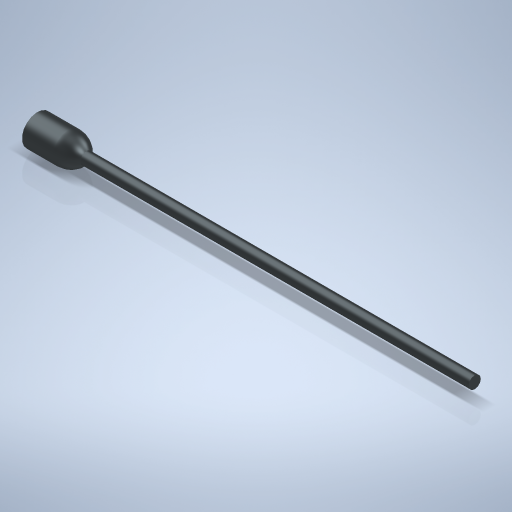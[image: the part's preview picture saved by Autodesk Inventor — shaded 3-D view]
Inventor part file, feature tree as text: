
AUTODESK INVENTOR PART (.ipt)
format: ipt  version: 2024 (Build 280153000, 153)  size: 276,480 bytes
history: native  units: mm
features: revolve x1, shell x1, sketch x1
ambient origin geometry x8: Origin, YZ Plane, XZ Plane, XY Plane, X Axis, Y Axis, Z Axis, Center Point
bodies: Volumenkörper1 (feature_tree)
feature tree (3):
  revolve  "Umdrehung1"
  shell  "Wandung1"  Thickness=4.0mm
  sketch  "Skizze1"  dims[d1=1.6mm d2=3.0mm d3=4.0mm d4=57.0mm d6=90.0deg d7=0.25mm]
